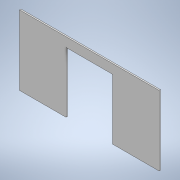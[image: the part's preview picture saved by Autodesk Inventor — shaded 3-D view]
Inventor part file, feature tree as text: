
AUTODESK INVENTOR PART (.ipt)
format: ipt  version: 2020 (Build 240168000, 168)  size: 94,720 bytes
history: native  units: in
note: dims shown in document units (in); Inventor stores cm internally (conversion verified against a paired STEP export)
features: extrude x1, sketch x1
ambient origin geometry x8: Origin, YZ Plane, XZ Plane, XY Plane, X Axis, Y Axis, Z Axis, Center Point
bodies: Solid1 (feature_tree)
feature tree (2):
  extrude  "Extrusion1"  Depth=5.9055in
  sketch  "Sketch1"  dims[d0=11.811in d1=5.9055in d2=3.937in d4=0.1181in d5=0.0in]
